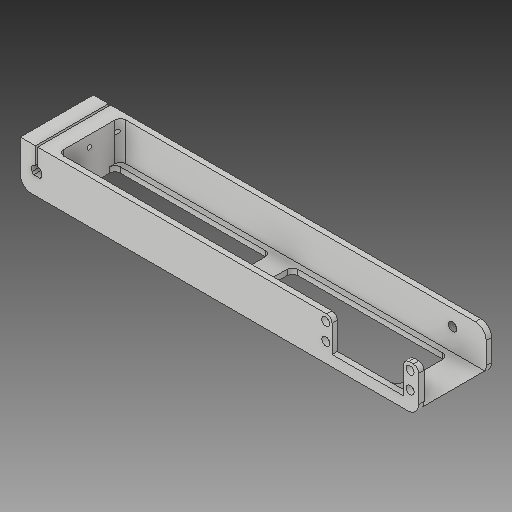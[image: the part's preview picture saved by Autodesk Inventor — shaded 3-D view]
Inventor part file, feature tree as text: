
AUTODESK INVENTOR PART (.ipt)
format: ipt  version: 2019 (Build 230136000, 136)  size: 310,784 bytes
history: native  units: in
note: dims shown in document units (in); Inventor stores cm internally (conversion verified against a paired STEP export)
features: sketch x7, projected_geometry x6, extrude x5, fillet x4, hole x3
ambient origin geometry x8: Origin, YZ Plane, XZ Plane, XY Plane, X Axis, Y Axis, Z Axis, Center Point
bodies: Solid1 (feature_tree)
feature tree (25):
  extrude  "Extrusion1"  Depth=1.685in
  extrude  "Extrusion2"  Depth=1.435in
  extrude  "Extrusion4"  Depth=0.125in TaperAngle=0.0deg
  extrude  "Extrusion5"  Depth=1.0in
  hole  "Hole1"  [1 undecoded]
  hole  "Hole2"  [1 undecoded]
  fillet  "Fillet1"  Radius=0.164in
  hole  "Hole3"  [1 undecoded]
  fillet  "Fillet2"  Radius=0.19in
  fillet  "Fillet3"  Radius=0.5in
  extrude  "Extrusion6"  Depth=0.125in
  fillet  "Fillet4"  Radius=0.361in
  sketch  "Sketch1"  dims[d0=1.0in d1=1.685in]
  sketch  "Sketch2"  dims[d2=0.875in d3=1.435in]
  projected_geometry  "Projected Loop1"
  projected_geometry  "Projected Loop2"
  sketch  "Sketch4"  dims[d4=0.125in d5=9.197in d6=0.0in]
  projected_geometry  "Projected Loop3"
  sketch  "Sketch5"  dims[d7=0.35in d8=1.0in]
  sketch  "Sketch6"  dims[d9=0.75in d10=2.0in]
  projected_geometry  "Projected Loop4"
  sketch  "Sketch7"  dims[d11=0.19in d12=0.19in d13=0.164in]
  projected_geometry  "Projected Loop5"
  sketch  "Sketch9"  dims[d14=0.3937in d15=0.19in d16=0.19in d19=0.5in d20=0.0in d22=0.776in d23=0.361in d26=0.75in d27=0.133in d28=0.078in d29=0.078in d30=0.098in d31=0.236in d32=0.0665in d33=0.0665in d34=0.0665in d35=0.0in d36=0.118in d37=0.133in d38=1.0in d39=0.5in d40=0.375in d41=0.05in d42=0.35in d43=1.685in d44=0.0in d45=0.75in d46=0.078in d47=0.078in d48=0.098in d49=0.0665in d50=0.0665in d51=0.0665in d52=0.0in d53=0.133in d54=1.0in d55=0.5in d56=0.375in d57=0.35in d58=0.133in d59=0.05in d60=1.685in d61=0.0in d62=0.25in d63=0.25in d64=1.685in d65=0.25in d66=0.8425in d67=0.2106in d68=0.2106in d69=0.158in d70=0.75in d71=0.375in d72=0.25in d73=0.5635in d74=0.355in d75=0.8108in d76=0.104in d77=0.276in d78=0.375in d79=0.25in d80=0.5635in d81=0.432in d82=0.8108in d83=0.125in d84=0.196in d85=0.5in d86=0.375in d87=0.25in d88=0.5635in d89=0.75in d90=0.8108in d91=1.9488in d92=1.9488in d93=0.164in d95=0.3937in d96=0.197in d97=0.197in d105=0.25in d106=0.125in d107=1.685in d108=8.697in d109=0.5in d110=0.25in d111=1.185in d112=3.5985in d113=1.0in d114=0.0in d115=0.5in d116=3.5985in d117=1.185in d118=0.25in d119=0.125in]
  projected_geometry  "Projected Loop7"
note: 3 required parameter values undecoded (feature->parameter linkage not recoverable at this tier; creation-order binding heuristic only, values carry confidence <= 0.55)
